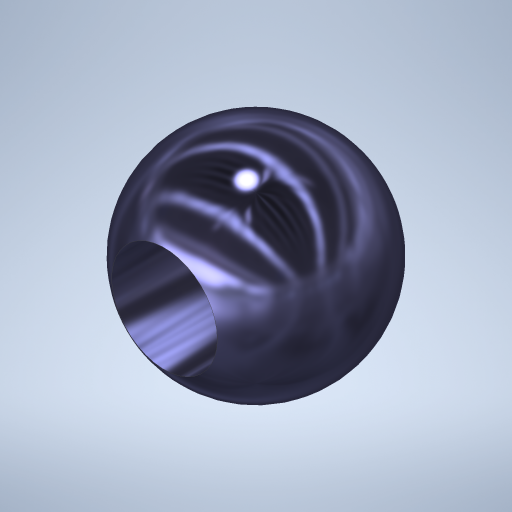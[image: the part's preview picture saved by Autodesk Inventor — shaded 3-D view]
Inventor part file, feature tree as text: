
AUTODESK INVENTOR PART (.ipt)
format: ipt  version: 2023.1 (Build 271208000, 208)  size: 337,408 bytes
history: native  units: in
note: dims shown in document units (in); Inventor stores cm internally (conversion verified against a paired STEP export)
features: sketch x1, revolve x1, extrude x1
ambient origin geometry x8: Origin, YZ Plane, XZ Plane, XY Plane, X Axis, Y Axis, Z Axis, Center Point
bodies: Solid1 (feature_tree)
feature tree (3):
  sketch  "Sketch1"  dims[d0=0.125in d1=0.25in d2=90.0deg d3=0.0in d4=0.0in]
  revolve  "Revolution1"  [1 undecoded]
  extrude  "Extrusion1"  TaperAngle=90.0deg  [1 undecoded]
note: 2 required parameter values undecoded (feature->parameter linkage not recoverable at this tier; creation-order binding heuristic only, values carry confidence <= 0.55)